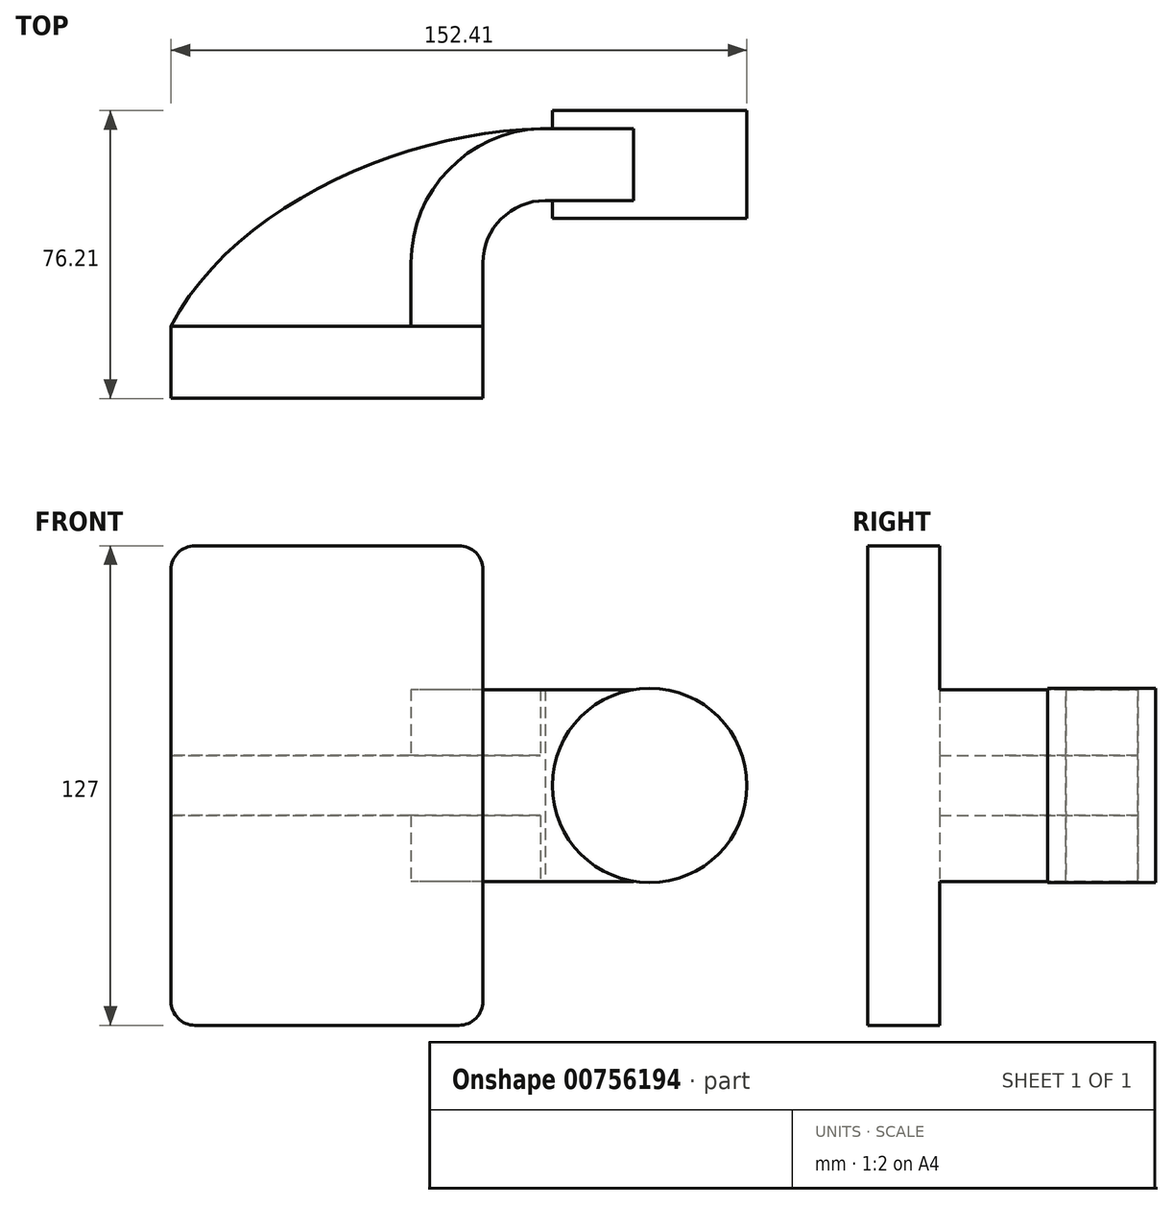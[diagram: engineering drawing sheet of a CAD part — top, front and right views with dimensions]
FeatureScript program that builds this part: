
annotation { "Feature Type Name" : "Feature", "Feature Type Description" : "" }
export const myFeature = defineFeature(function(context is Context, id is Id, definition is map)
    precondition{}
    {
        {
            var Q0;
            Q0=qCreatedBy(makeId("Top.planeOp"),FACE);
            var sketch = newSketch(context, id + "F0", { "sketchPlane" : qUnion([Q0])});
            skLineSegment(sketch, "E0.bottom", {"start": v(41.27, 9.53) * mm, "end": v(-41.28, 9.53) * mm});
            skLineSegment(sketch, "E0.top", {"start": v(41.28, -9.52) * mm, "end": v(-41.27, -9.52) * mm});
            skLineSegment(sketch, "E0.left", {"start": v(41.27, 9.53) * mm, "end": v(41.28, -9.52) * mm});
            skLineSegment(sketch, "E0.right", {"start": v(-41.28, 9.53) * mm, "end": v(-41.27, -9.53) * mm});
            skPoint(sketch, "E0.middle", {"position": v(0, 0) * mm});
            skLineSegment(sketch, "E1.bottom", {"start": v(111.12, 66.68) * mm, "end": v(60.32, 66.68) * mm});
            skLineSegment(sketch, "E1.top", {"start": v(111.12, 38.1) * mm, "end": v(60.32, 38.1) * mm});
            skLineSegment(sketch, "E1.left", {"start": v(111.12, 66.68) * mm, "end": v(111.12, 38.1) * mm});
            skLineSegment(sketch, "E1.right", {"start": v(60.32, 66.68) * mm, "end": v(60.32, 38.1) * mm});
            skPoint(sketch, "E1.middle", {"position": v(85.72, 52.39) * mm});
            skLineSegment(sketch, "E2", {"start": v(41.27, 9.53) * mm, "end": v(41.27, 26.37) * mm});
            skArc(sketch, "E3", {"start": v(41.27, 26.37) * mm, "mid": v(46.11, 38.04) * mm, "end": v(57.78, 42.88) * mm});
            skLineSegment(sketch, "E4", {"start": v(57.78, 42.88) * mm, "end": v(85.38, 42.88) * mm});
            skLineSegment(sketch, "E5.0", {"start": v(57.78, 61.93) * mm, "end": v(85.38, 61.93) * mm});
            skArc(sketch, "E5.1", {"start": v(22.22, 26.37) * mm, "mid": v(32.64, 51.5) * mm, "end": v(57.78, 61.93) * mm});
            skLineSegment(sketch, "E5.2", {"start": v(22.22, 9.53) * mm, "end": v(22.22, 26.37) * mm});
            skFitSpline(sketch, "E6", {"points": [v(-41.28, 9.53) * mm, v(57.78, 61.93) * mm], "startDerivative": vector(49.02, 96.39) * mm, "endDerivative": vector(110.58, 1.36) * mm});
            skLineSegment(sketch, "E7", {"start": v(85.38, 66.68) * mm, "end": v(85.38, 38.1) * mm});
            skPoint(sketch, "E7.startSnap0", {"position": v(85.72, 66.68) * mm});
            skSolve(sketch);
        }
        {
            var Q0;
            Q0=makeQuery(id+"F0.imprint","IMPRINT",FACE,{"disambiguationData":[TD([[makeQuery(id+"F0.imprint","IMPRINT",EDGE,{"derivedFrom":sQuery(id+"F0.wireOp",EDGE,"E0.top")}),-1.0]])]});
            extrude(context, id + "F1", {"entities" : qUnion([Q0]), "endBound" : BoundingType.SYMMETRIC, "depth" : 127 * mm, "offsetDistance" : 25.4 * mm});
        }
        {
            var Q0;
            {var subQ0=sQuery(id+"F0.wireOp",EDGE,"E5.0");var subQ1=sQuery(id+"F0.wireOp",EDGE,"E1.right");var subQ2=makeQuery(id+"F0.imprint","INTERSECT",VERTEX,{"derivedFrom":[subQ1,subQ0]});Q0=makeQuery(id+"F0.imprint","IMPRINT",FACE,{"disambiguationData":[TD([[makeQuery(id+"F0.imprint","IMPRINT",EDGE,{"disambiguationData":[TD([[subQ2,-1.0]])],"derivedFrom":subQ1}),1.0]])]});}
            var Q1;
            {var subQ1=sQuery(id+"F0.wireOp",EDGE,"E2");Q1=makeQuery(id+"F0.imprint","IMPRINT",FACE,{"disambiguationData":[TD([[makeQuery(id+"F0.imprint","IMPRINT",EDGE,{"derivedFrom":subQ1}),1.0]])]});}
            extrude(context, id + "F2", {"entities" : qUnion([Q0, Q1]), "operationType" : NewBodyOperationType.ADD, "endBound" : BoundingType.SYMMETRIC, "depth" : 50.8 * mm, "offsetDistance" : 25.4 * mm});
        }
        {
            var Q0;
            {var subQ3=sQuery(id+"F0.wireOp",EDGE,"E5.2");Q0=makeQuery(id+"F0.imprint","IMPRINT",FACE,{"disambiguationData":[TD([[makeQuery(id+"F0.imprint","IMPRINT",EDGE,{"derivedFrom":subQ3}),1.0]])]});}
            extrude(context, id + "F3", {"entities" : qUnion([Q0]), "operationType" : NewBodyOperationType.ADD, "endBound" : BoundingType.SYMMETRIC, "depth" : 15.88 * mm, "offsetDistance" : 25.4 * mm});
        }
        {
            var Q0;
            {var subQ4=sQuery(id+"F0.wireOp",EDGE,"E1.left");Q0=makeQuery(id+"F0.imprint","IMPRINT",FACE,{"disambiguationData":[TD([[makeQuery(id+"F0.imprint","IMPRINT",EDGE,{"derivedFrom":subQ4}),-1.0]])]});}
            var Q1;
            Q1=sQuery(id+"F0.wireOp",EDGE,"E7");
            revolve(context, id + "F4", {"operationType" : NewBodyOperationType.ADD, "surfaceOperationType" : NewSurfaceOperationType.NEW, "entities" : qUnion([Q0]), "axis" : qUnion([Q1]), "revolveType" : RevolveType.FULL});
        }
        {
            var Q0;
            Q0=makeQuery(id+"F1.opExtrude","CAP_EDGE",EDGE,{"disambiguationData":[OSD([sQuery(id+"F0.wireOp",EDGE,"E0.left")])],"isStart":false});
            var Q1;
            Q1=makeQuery(id+"F1.opExtrude","CAP_EDGE",EDGE,{"disambiguationData":[OSD([sQuery(id+"F0.wireOp",EDGE,"E0.right")])],"isStart":false});
            var Q2;
            Q2=makeQuery(id+"F1.opExtrude","CAP_EDGE",EDGE,{"disambiguationData":[OSD([sQuery(id+"F0.wireOp",EDGE,"E0.left")])],"isStart":true});
            var Q3;
            Q3=makeQuery(id+"F1.opExtrude","CAP_EDGE",EDGE,{"disambiguationData":[OSD([sQuery(id+"F0.wireOp",EDGE,"E0.right")])],"isStart":true});
            fillet(context, id + "F5", {"entities" : qUnion([Q0, Q1, Q2, Q3]), "radius" : 6.35 * mm, "tangentPropagation" : true, "allowEdgeOverflow" : false});
        }
    });
